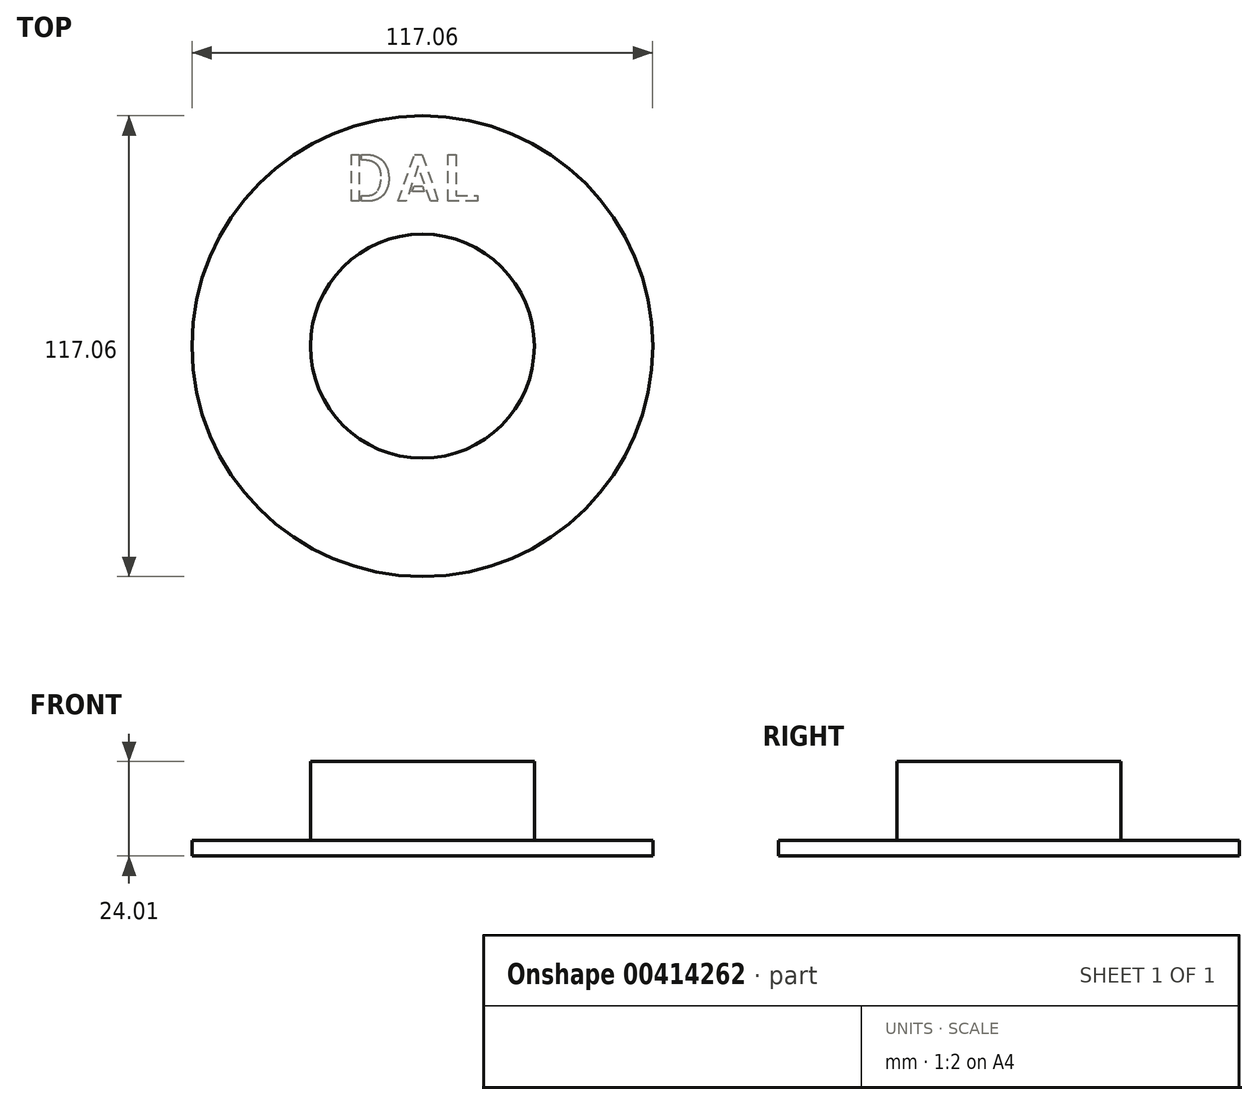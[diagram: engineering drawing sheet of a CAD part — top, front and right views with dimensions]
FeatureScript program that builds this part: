
annotation { "Feature Type Name" : "Feature", "Feature Type Description" : "" }
export const myFeature = defineFeature(function(context is Context, id is Id, definition is map)
    precondition{}
    {
        {
            var Q0;
            Q0=qCreatedBy(makeId("Top.planeOp"),FACE);
            var sketch = newSketch(context, id + "F0", { "sketchPlane" : qUnion([Q0])});
            skCircle(sketch, "E0", {"center": v(0, 0) * mm, "radius": 58.53 * mm});
            skSolve(sketch);
        }
        {
            var Q0;
            Q0=makeQuery(id+"F0.imprint","IMPRINT",FACE,{"disambiguationData":[TD([[makeQuery(id+"F0.imprint","IMPRINT",EDGE,{"derivedFrom":sQuery(id+"F0.wireOp",EDGE,"E0")}),1.0]])]});
            var Q1;
            Q1=sQuery(id+"F0.wireOp",EDGE,"E0");
            extrude(context, id + "F1", {"entities" : qUnion([Q0]), "surfaceEntities" : qUnion([Q1]), "depth" : 4 * mm});
        }
        {
            var Q0;
            Q0=makeQuery(id+"F1.opExtrude","CAP_FACE",FACE,{"disambiguationData":[OSD([sQuery(id+"F0.wireOp",EDGE,"E0")])],"isStart":false});
            var sketch = newSketch(context, id + "F2", { "sketchPlane" : qUnion([Q0])});
            skCircle(sketch, "E1", {"center": v(0, 0) * mm, "radius": 28.45 * mm});
            skSolve(sketch);
        }
        {
            var Q0;
            Q0=makeQuery(id+"F2.imprint","IMPRINT",FACE,{"disambiguationData":[TD([[makeQuery(id+"F2.imprint","IMPRINT",EDGE,{"derivedFrom":sQuery(id+"F2.wireOp",EDGE,"E1")}),1.0]])]});
            var Q1;
            Q1=sQuery(id+"F2.wireOp",EDGE,"E1");
            extrude(context, id + "F3", {"entities" : qUnion([Q0]), "operationType" : NewBodyOperationType.ADD, "surfaceEntities" : qUnion([Q1]), "depth" : 20 * mm});
        }
        {
            var Q0;
            Q0=makeQuery(id+"F1.opExtrude","CAP_FACE",FACE,{"disambiguationData":[OSD([sQuery(id+"F0.wireOp",EDGE,"E0")])],"isStart":false});
            var sketch = newSketch(context, id + "F4", { "sketchPlane" : qUnion([Q0])});
            skText(sketch, "E2", { "text": "DAL", "fontName": "AllertaStencil-Regular.ttf"});
            const initialGuessF4  = {"E2": [-0.01959, 0.03685, 1, 0, 0.01188]};
            skSetInitialGuess(sketch, initialGuessF4);
            skSolve(sketch);
        }
        {
            var Q0;
            Q0 = qSketchRegion(id + "F4", true);
            extrude(context, id + "F5", {"entities" : qUnion([Q0]), "operationType" : NewBodyOperationType.ADD, "oppositeDirection" : true, "depth" : 4 * mm});
        }
    });
